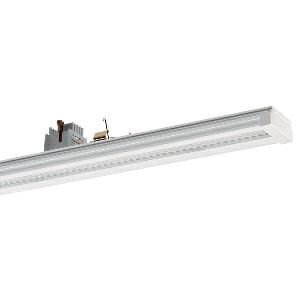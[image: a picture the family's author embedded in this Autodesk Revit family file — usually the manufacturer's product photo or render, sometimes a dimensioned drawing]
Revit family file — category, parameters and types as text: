
# Revit family: conveo_-_cvg_8000_840_w-l_ea_5_226848339-00804972_b808
name_source: partatom
category: Lighting Fixtures
units: mm (PartAtom-declared; Revit-internal decimal feet)

## family parameters
Cut with Voids When Loaded = No
Host = Face
Light Source = No
Part Type = Normal
Room Calculation Point = No
Round Connector Dimension = Use Diameter
Shared = No

## types (1)
- CONVEO - CVG 8000/840/W-L/EA/5 (1 x LED, 8100 lm, 4000K)
    Apparent Load = 47 VA
    Approval mark = CE
    CIE Flux Codes = 85 97 99 100 100
    Color Rendering = 80-89
    Color Temperature = 4000K
    Control Gear = Electronic ballast
    Default Elevation = 1800 mm
    Description = CVG 8000/840/W-L/EA/5|Continuous-row system|light source: LED|work equipment: Electronic ballast|connected load: 220-240 V, 50-60 Hz|Power consumption: approx. 47 W|luminous flux: 8100 lm|luminous efficacy: 172 lm/W|colour temperature: Cold white, ca. 4000 K|color rendering index (CRI): >= 80|chromaticity tolerance:  3 SDCM|System of protection: IP 54|class of protection: I|technology: Switchable|luminaire body|material: Aluminium|surface: Powder coatet|colour: White|lamp cover: Acrylic (PMMA), Satine|weight (net): approx. 1.9 kg|Fastening: Available separately|maximum ambient temperature: 46 ░C|glare control: Lens optics|Approval mark: VDE - ENEC|
    Frequency = 50 Hz
    Height = 70 mm
    Lamp = 1 x LED
    Lamp Light Flux = 8100 lm
    Lamp count = 1
    Length = 1500 mm
    Luminous efficacy = 172 lm/W
    Manufacturer = Waldmann
    ModVariant = No
    Model = 226848339-00804972
    Mounting Place = Ceiling
    Mounting Type = Pendant
    Number of Poles = 1
    OnlyDefault = Yes
    Power Factor = 1
    Product Name = CONVEO - CVG 8000/840/W-L/EA/5
    Product group = Continuous-row system (industry)
    ProductGroupID = 301
    Protection Class = Protection class I
    Protection Degree = IP 54
    RLX_Detail_Level = 1
    RlxData = <blob elided: 99613 chars, md5=ca67e84c>
    Socket = socket
    Standby Power = 0 W
    System Light Flux = 8100 lm
    System Power = 47 W
    Type Comments = Product without accessories
    Type Image = 226848319-00804970_1l5.jpg
    URL = http://relux.com
    VarID = ---
    Voltage = 230 V
    Voltage Range = 220-240 V
    Weight = 0.00 kg
    Width = 64 mm

## geometry (parser evidence)
native form markers: Blend x4, Sweep x11
no freeform markers — native parametric forms only
